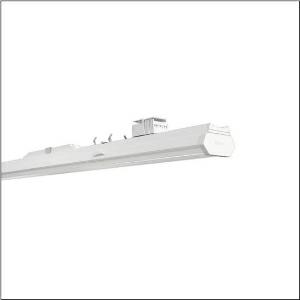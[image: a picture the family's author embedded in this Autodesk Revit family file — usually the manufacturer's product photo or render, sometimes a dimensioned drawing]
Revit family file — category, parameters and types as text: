
# Revit family: licross_r__21_protected_mo_52td1bvn465g_e1b8
name_source: partatom
category: Lighting Fixtures
units: mm (PartAtom-declared; Revit-internal decimal feet)

## family parameters
Cut with Voids When Loaded = No
Host = Face
Light Source = No
Part Type = Normal
Room Calculation Point = No
Round Connector Dimension = Use Diameter
Shared = No

## types (1)
- --- (1 x LED, 6500 lm, 39 W, 4000K)
    Apparent Load = 39 VA
    CIE Flux Codes = 54 82 95 97 100
    Color Rendering = 80
    Color Temperature = 4000K
    Default Elevation = 1800 mm
    Description = Licross® 21 Protected MO, luminaire insert, of sheet steel, galvanised, coil coated, white, length: 1.500mm, width: 90mm, height: 101mm, LED rated luminous flux: 6.500lm, light colour: 840, control gear: DALI 2, CLO, with plug, 5-pole, with phase selection, mains connection: 220..240V, AC, 50/60Hz, start of lifetime: 39W, end of service life: 46W, halogen-free wiring, primary optical cover: cover, of PMMA, light emission: direct distribution, primary light characteristic: symmetric, protection rating (complete): IP54, insulation class (complete): insulation class I (protective earthing), certification: CE, ENEC, VDE, UKCA, protection symbol: D if used in an environment with non-conductive dust loads with corresponding accessories, impact resistance: IK06, permissible ambient temperature for indoor applications: -25..+45°C, corresponds to IFS (International Featured Standards) requirements for safety and quality in the food industry, reducing of maximum allowable ambient temperature of 5°C with ceiling mounting, LABS conformity tested according to VDMA 24364:2018-05, packaging unit: 1 piece
    Height = 92 mm
    Lamp = 1 x LED
    Lamp Light Flux = 6500 lm
    Lamp Power = 39 W
    Lamp count = 1
    Length = 1500 mm
    Luminous efficacy = 167 lm/W
    Manufacturer = Siteco
    ModVariant = No
    Model = 52TD1BVN465G
    Mounting Place = Ceiling
    Mounting Type = Pendant
    Number of Poles = 1
    OnlyDefault = Yes
    Power Factor = 1
    Product Name = Licross® 21 Protected MO
    Product group = luminaire insert
    ProductGroupID = 902
    Protection Class = Protection class I
    Protection Degree = IP 54
    RLX_Detail_Level = 1
    RLX_Emergency_Light_Flux = 0 lm
    RLX_Emergency_Type = 0
    RLX_Emergency_Type_DB = No
    RlxData = <blob elided: 24449 chars, md5=7416ce2e>
    Socket = socket
    Standby Power = 0 W
    System Light Flux = 6500 lm
    System Power = 39 W
    Type Comments = factory setting: luminous flux: 100 % | dim-lin: 254 | 262 mA
    Type Image = l_1256148.jpg
    URL = http://relux.com
    VarID = @adj_082822
    Voltage = 0 V
    Weight = 0.00 kg
    Width = 88 mm

## geometry (parser evidence)
native form markers: Blend x4, Sweep x12
no freeform markers — native parametric forms only
